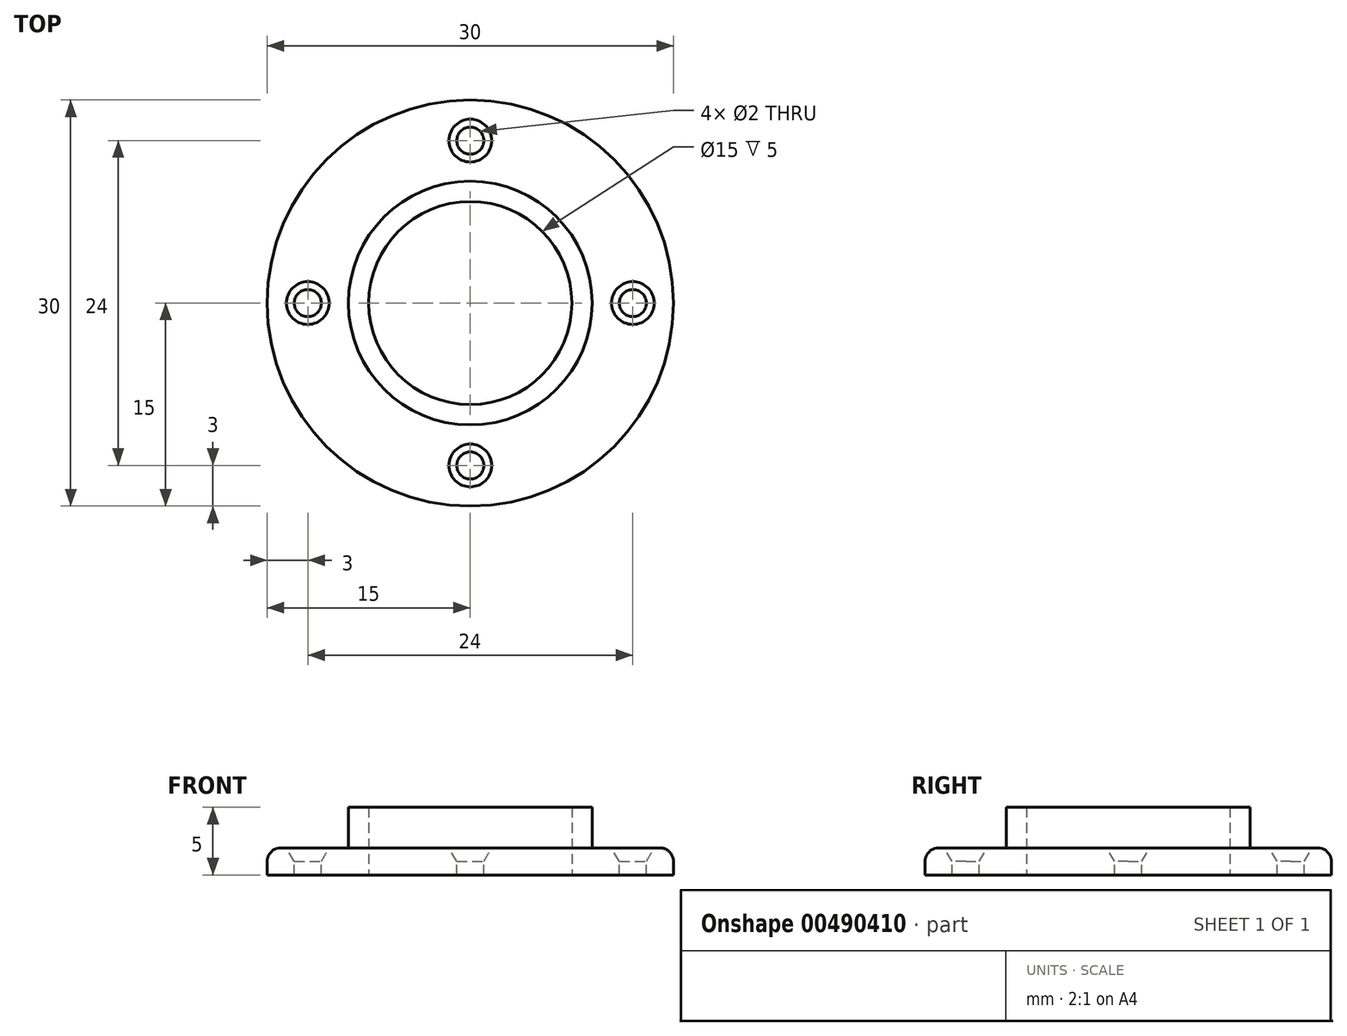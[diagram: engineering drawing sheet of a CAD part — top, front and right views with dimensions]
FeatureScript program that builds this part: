
annotation { "Feature Type Name" : "Feature", "Feature Type Description" : "" }
export const myFeature = defineFeature(function(context is Context, id is Id, definition is map)
    precondition{}
    {
        {
            var Q0;
            Q0=qCreatedBy(makeId("Top.planeOp"),FACE);
            var sketch = newSketch(context, id + "F0", { "sketchPlane" : qUnion([Q0])});
            skCircle(sketch, "E0", {"center": v(0, 0) * mm, "radius": 15 * mm});
            skSolve(sketch);
        }
        {
            var Q0;
            Q0=makeQuery(id+"F0.imprint","IMPRINT",FACE,{"disambiguationData":[TD([[makeQuery(id+"F0.imprint","IMPRINT",EDGE,{"derivedFrom":sQuery(id+"F0.wireOp",EDGE,"E0")}),1.0]])]});
            extrude(context, id + "F1", {"entities" : qUnion([Q0]), "depth" : 1 * mm, "hasSecondDirection" : true, "secondDirectionOppositeDirection" : true, "secondDirectionDepth" : 1 * mm});
        }
        {
            var Q0;
            Q0=qCreatedBy(makeId("Top.planeOp"),FACE);
            var sketch = newSketch(context, id + "F2", { "sketchPlane" : qUnion([Q0])});
            skCircle(sketch, "E1", {"center": v(12, 0) * mm, "radius": 1 * mm});
            skCircle(sketch, "E2.1.0", {"center": v(0, 12) * mm, "radius": 1 * mm});
            skCircle(sketch, "E2.2.0", {"center": v(-12, 0) * mm, "radius": 1 * mm});
            skCircle(sketch, "E2.3.0", {"center": v(0, -12) * mm, "radius": 1 * mm});
            skPoint(sketch, "E2.center", {"position": v(0, 0) * mm});
            skSolve(sketch);
        }
        {
            var Q0;
            Q0 = qSketchRegion(id + "F2", true);
            extrude(context, id + "F3", {"entities" : qUnion([Q0]), "operationType" : NewBodyOperationType.REMOVE, "oppositeDirection" : true, "depth" : 2 * mm, "hasSecondDirection" : true, "secondDirectionOppositeDirection" : false, "secondDirectionDepth" : 2 * mm, "hasSecondDirectionDraft" : true, "secondDirectionDraftAngle" : 30 * degree});
        }
        {
            var Q0;
            Q0=makeQuery(id+"F1.opExtrude","CAP_FACE",FACE,{"disambiguationData":[OSD([sQuery(id+"F0.wireOp",EDGE,"E0")])],"isStart":false});
            var sketch = newSketch(context, id + "F4", { "sketchPlane" : qUnion([Q0])});
            skCircle(sketch, "E3", {"center": v(0, 0) * mm, "radius": 9 * mm});
            skCircle(sketch, "E4", {"center": v(0, 0) * mm, "radius": 7.5 * mm});
            skSolve(sketch);
        }
        {
            var Q0;
            Q0=makeQuery(id+"F4.imprint","IMPRINT",FACE,{"disambiguationData":[TD([[makeQuery(id+"F4.imprint","IMPRINT",EDGE,{"derivedFrom":sQuery(id+"F4.wireOp",EDGE,"E3")}),1.0]])]});
            extrude(context, id + "F5", {"entities" : qUnion([Q0]), "operationType" : NewBodyOperationType.ADD, "depth" : 3 * mm});
        }
        {
            var Q0;
            Q0=makeQuery(id+"F5.boolean.opBoolean","SPLIT",FACE,{"disambiguationData":[TD([makeQuery(id+"F5.opExtrude","SWEPT_FACE",FACE,{"disambiguationData":[OSD([sQuery(id+"F4.wireOp",EDGE,"E4")])]})])],"derivedFrom":makeQuery(id+"F1.opExtrude","CAP_FACE",FACE,{"disambiguationData":[OSD([sQuery(id+"F0.wireOp",EDGE,"E0")])],"isStart":false})});
            extrude(context, id + "F6", {"entities" : qUnion([Q0]), "operationType" : NewBodyOperationType.REMOVE, "oppositeDirection" : true, "depth" : 5 * mm});
        }
        {
            var Q0;
            Q0=makeQuery(id+"F1.opExtrude","CAP_EDGE",EDGE,{"disambiguationData":[OSD([sQuery(id+"F0.wireOp",EDGE,"E0")])],"isStart":false});
            var Q1;
            Q1=makeQuery(id+"F5.opExtrude","CAP_EDGE",EDGE,{"disambiguationData":[OSD([sQuery(id+"F4.wireOp",EDGE,"E3")])],"isStart":true});
            fillet(context, id + "F7", {"entities" : qUnion([Q0, Q1]), "radius" : 1 * mm, "tangentPropagation" : true, "allowEdgeOverflow" : false});
        }
    });
